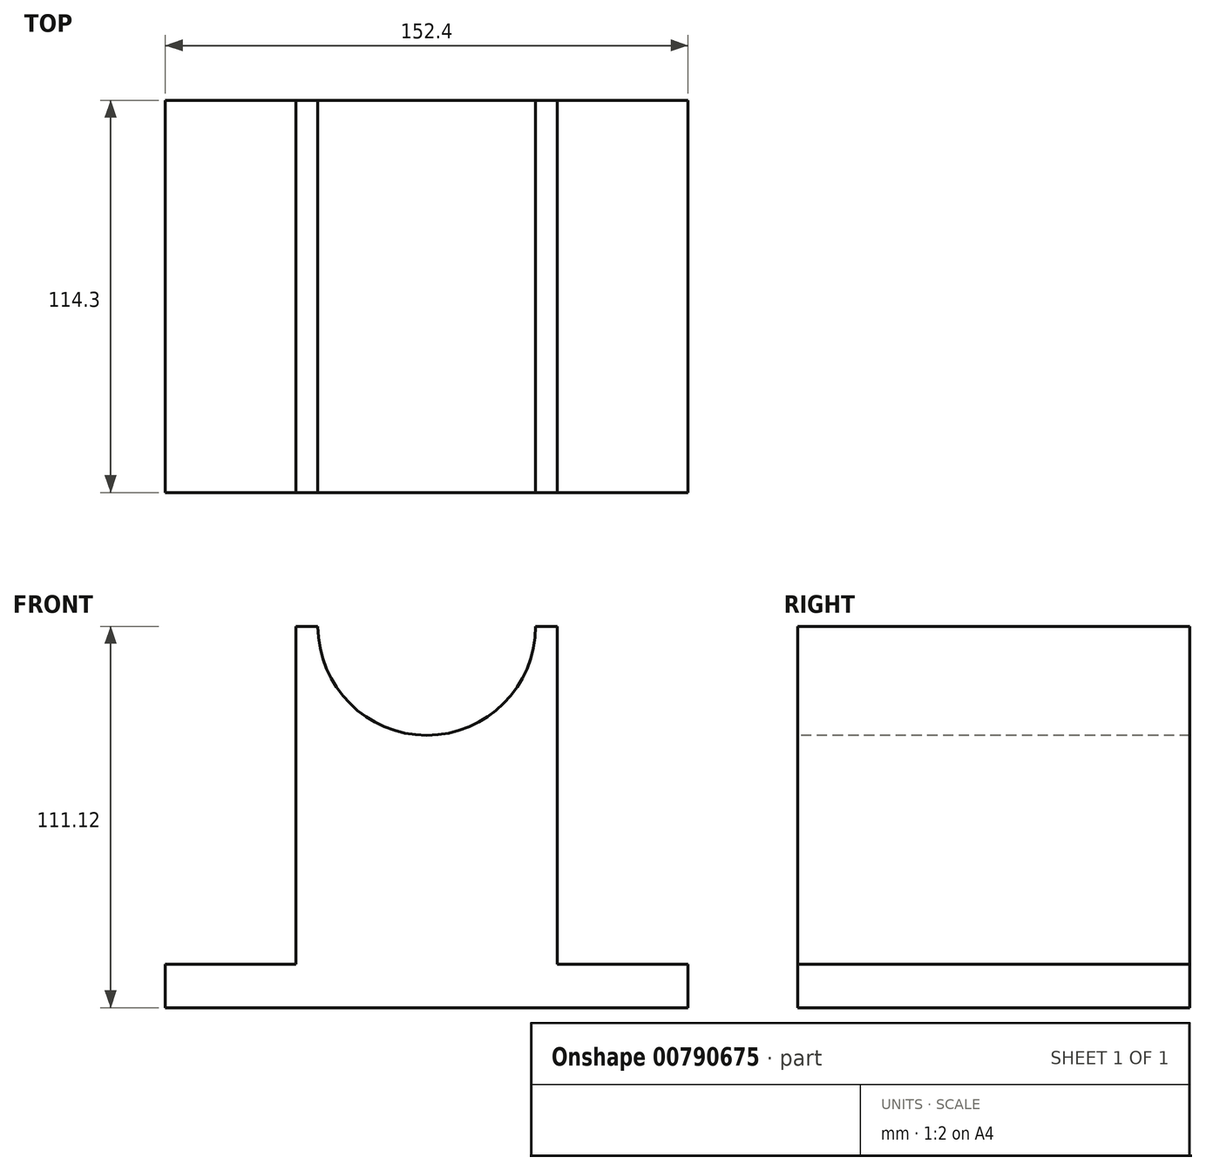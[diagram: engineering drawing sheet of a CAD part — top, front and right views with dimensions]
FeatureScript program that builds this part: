
annotation { "Feature Type Name" : "Feature", "Feature Type Description" : "" }
export const myFeature = defineFeature(function(context is Context, id is Id, definition is map)
    precondition{}
    {
        {
            var Q0;
            Q0=qCreatedBy(makeId("Front.planeOp"),FACE);
            var sketch = newSketch(context, id + "F0", { "sketchPlane" : qUnion([Q0])});
            skLineSegment(sketch, "E0", {"start": v(0, 0) * mm, "end": v(-76.2, 0) * mm});
            skLineSegment(sketch, "E1", {"start": v(0, 0) * mm, "end": v(76.2, 0) * mm});
            skLineSegment(sketch, "E2", {"start": v(-76.2, 0) * mm, "end": v(-76.2, 12.7) * mm});
            skLineSegment(sketch, "E3", {"start": v(-76.2, 12.7) * mm, "end": v(-38.1, 12.7) * mm});
            skLineSegment(sketch, "E4", {"start": v(-38.1, 12.7) * mm, "end": v(-38.1, 111.13) * mm});
            skLineSegment(sketch, "E5", {"start": v(-38.1, 111.13) * mm, "end": v(38.1, 111.13) * mm});
            skLineSegment(sketch, "E6", {"start": v(38.1, 111.13) * mm, "end": v(38.1, 12.7) * mm});
            skLineSegment(sketch, "E7", {"start": v(38.1, 12.7) * mm, "end": v(76.2, 12.7) * mm});
            skLineSegment(sketch, "E8", {"start": v(76.2, 12.7) * mm, "end": v(76.2, 0) * mm});
            skSolve(sketch);
        }
        {
            var Q0;
            Q0=makeQuery(id+"F0.imprint","IMPRINT",FACE,{"disambiguationData":[TD([[makeQuery(id+"F0.imprint","IMPRINT",EDGE,{"derivedFrom":sQuery(id+"F0.wireOp",EDGE,"E0")}),-1.0]])]});
            extrude(context, id + "F1", {"entities" : qUnion([Q0]), "depth" : 114.3 * mm, "offsetDistance" : 25.4 * mm});
        }
        {
            var Q0;
            Q0=makeQuery(id+"F1.opExtrude","CAP_FACE",FACE,{"disambiguationData":[OSD([sQuery(id+"F0.wireOp",EDGE,"E0"),sQuery(id+"F0.wireOp",EDGE,"E1"),sQuery(id+"F0.wireOp",EDGE,"E2"),sQuery(id+"F0.wireOp",EDGE,"E3"),sQuery(id+"F0.wireOp",EDGE,"E4"),sQuery(id+"F0.wireOp",EDGE,"E5"),sQuery(id+"F0.wireOp",EDGE,"E6"),sQuery(id+"F0.wireOp",EDGE,"E7"),sQuery(id+"F0.wireOp",EDGE,"E8")])],"isStart":false});
            var sketch = newSketch(context, id + "F2", { "sketchPlane" : qUnion([Q0])});
            skLineSegment(sketch, "E9", {"start": v(0, 111.13) * mm, "end": v(-31.75, 111.13) * mm, "construction": true});
            skLineSegment(sketch, "E10", {"start": v(0, 111.13) * mm, "end": v(31.75, 111.13) * mm, "construction": true});
            skArc(sketch, "E11", {"start": v(-31.75, 111.13) * mm, "mid": v(0, 79.38) * mm, "end": v(31.75, 111.13) * mm});
            skSolve(sketch);
        }
        {
            var Q0;
            {var subQ0=sQuery(id+"F2.wireOp",EDGE,"E11");Q0=makeQuery(id+"F2.imprint","IMPRINT",FACE,{"disambiguationData":[TD([[makeQuery(id+"F2.imprint","IMPRINT",EDGE,{"derivedFrom":subQ0}),1.0]])]});}
            extrude(context, id + "F3", {"entities" : qUnion([Q0]), "operationType" : NewBodyOperationType.REMOVE, "endBound" : BoundingType.THROUGH_ALL, "oppositeDirection" : true, "depth" : 25.4 * mm, "offsetDistance" : 25.4 * mm});
        }
    });
